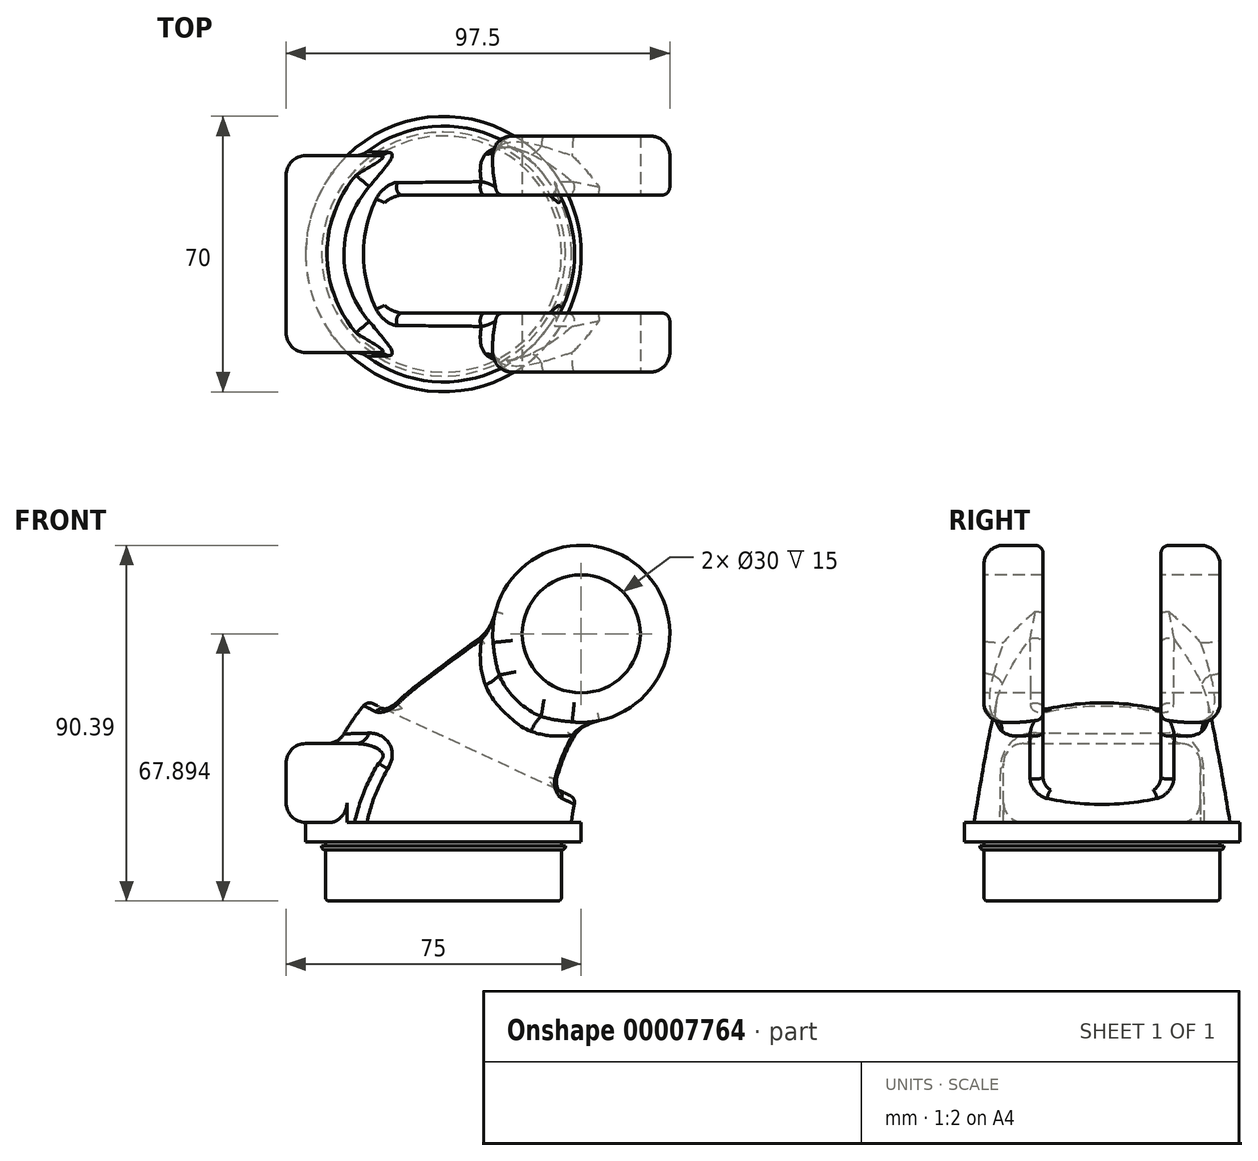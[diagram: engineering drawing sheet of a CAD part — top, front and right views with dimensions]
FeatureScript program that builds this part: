
annotation { "Feature Type Name" : "Feature", "Feature Type Description" : "" }
export const myFeature = defineFeature(function(context is Context, id is Id, definition is map)
    precondition{}
    {
        {
            var Q0;
            Q0=qCreatedBy(makeId("Top.planeOp"),FACE);
            var sketch = newSketch(context, id + "F0", { "sketchPlane" : qUnion([Q0])});
            skCircle(sketch, "E0", {"center": v(0, 0) * mm, "radius": 35 * mm});
            skSolve(sketch);
        }
        {
            var Q0;
            Q0 = qSketchRegion(id + "F0", true);
            extrude(context, id + "F1", {"entities" : qUnion([Q0]), "depth" : 5 * mm});
        }
        {
            var Q0;
            Q0=qCreatedBy(makeId("Front.planeOp"),FACE);
            var sketch = newSketch(context, id + "F2", { "sketchPlane" : qUnion([Q0])});
            skArc(sketch, "E1", {"start": v(17.6, 38.3) * mm, "mid": v(5.55, 23.37) * mm, "end": v(0, 5) * mm});
            skLineSegment(sketch, "E2", {"start": v(17.6, 38.3) * mm, "end": v(35, 52.9) * mm});
            skSolve(sketch);
        }
        {
            var Q0;
            Q0=sQuery(id+"F2.wireOp",EDGE,"E2");
            var Q1;
            Q1=sQuery(id+"F2.wireOp",VERTEX,"E2.end");
            cPlane(context, id + "F3", {"entities" : qUnion([Q0, Q1]), "cplaneType" : CPlaneType.LINE_POINT, "offset" : 150 * mm, "width" : 150 * mm, "height" : 150 * mm});
        }
        {
            var Q0;
            Q0=makeQuery(id+"F1.opExtrude","CAP_FACE",FACE,{"disambiguationData":[OSD([sQuery(id+"F0.wireOp",EDGE,"E0")])],"isStart":false});
            var sketch = newSketch(context, id + "F4", { "sketchPlane" : qUnion([Q0])});
            skCircle(sketch, "E3", {"center": v(0, 0) * mm, "radius": 32.5 * mm});
            skSolve(sketch);
        }
        {
            var Q0;
            Q0=qCreatedBy(id+"F3.planeOp",FACE);
            var sketch = newSketch(context, id + "F5", { "sketchPlane" : qUnion([Q0])});
            skCircle(sketch, "E4", {"center": v(0, 18.02) * mm, "radius": 22.5 * mm});
            skSolve(sketch);
        }
        {
            var Q0;
            Q0=qCreatedBy(makeId("Front.planeOp"),FACE);
            var sketch = newSketch(context, id + "F6", { "sketchPlane" : qUnion([Q0])});
            skArc(sketch, "E5", {"start": v(-13.25, 41.78) * mm, "mid": v(-26.5, 25.3) * mm, "end": v(-32.5, 5) * mm});
            skLineSegment(sketch, "E6", {"start": v(-13.25, 41.78) * mm, "end": v(20.54, 70.13) * mm});
            skSolve(sketch);
        }
        {
            var Q0;
            Q0=qCreatedBy(makeId("Front.planeOp"),FACE);
            var sketch = newSketch(context, id + "F7", { "sketchPlane" : qUnion([Q0])});
            skArc(sketch, "E7", {"start": v(48.46, 34.82) * mm, "mid": v(37.6, 21.45) * mm, "end": v(32.5, 5) * mm});
            skLineSegment(sketch, "E8", {"start": v(48.46, 34.82) * mm, "end": v(49.46, 35.66) * mm});
            skSolve(sketch);
        }
        {
            var Q1;
            Q1=makeQuery(id+"F4.imprint","IMPRINT",FACE,{"disambiguationData":[TD([[makeQuery(id+"F4.imprint","IMPRINT",EDGE,{"derivedFrom":sQuery(id+"F4.wireOp",EDGE,"E3")}),1.0]])]});
            var Q2;
            Q2=makeQuery(id+"F5.imprint","IMPRINT",FACE,{"disambiguationData":[TD([[makeQuery(id+"F5.imprint","IMPRINT",EDGE,{"derivedFrom":sQuery(id+"F5.wireOp",EDGE,"E4")}),1.0]])]});
            var Q3;
            Q3 = qBodyType(qCreatedBy(id + "F6" ,EDGE), BodyType.WIRE);
            var Q4;
            Q4 = qBodyType(qCreatedBy(id + "F7" ,EDGE), BodyType.WIRE);
            loft(context, id + "F8", {"operationType" : NewBodyOperationType.ADD, "addGuides" : true, "sheetProfilesArray" : [{ "sheetProfileEntities" : qUnion([Q1]) }, { "sheetProfileEntities" : qUnion([Q2]) }], "guidesArray" : [{ "guideEntities" : qUnion([Q3]), "guideDerivativeType" : LoftGuideDerivativeType.DEFAULT, "guideDerivativeMagnitude" : 1 }, { "guideEntities" : qUnion([Q4]), "guideDerivativeType" : LoftGuideDerivativeType.DEFAULT, "guideDerivativeMagnitude" : 1 }]});
        }
        {
            var Q0;
            Q0=qCreatedBy(makeId("Front.planeOp"),FACE);
            var sketch = newSketch(context, id + "F9", { "sketchPlane" : qUnion([Q0])});
            skLineSegment(sketch, "E9", {"start": v(20.54, 70.13) * mm, "end": v(49.46, 35.66) * mm, "construction": true});
            skCircle(sketch, "E10", {"center": v(35, 52.9) * mm, "radius": 22.5 * mm});
            skSolve(sketch);
        }
        {
            var Q0;
            Q0 = qSketchRegion(id + "F9", true);
            extrude(context, id + "F10", {"entities" : qUnion([Q0]), "operationType" : NewBodyOperationType.ADD, "endBound" : BoundingType.SYMMETRIC, "depth" : 60 * mm});
        }
        {
            var Q0;
            Q0=makeQuery(id+"F10.boolean.opBoolean","INTERSECT",EDGE,{"derivedFrom":[makeQuery(id+"F8.opLoft","SWEPT_FACE",FACE,{"disambiguationData":[OSD([sQuery(id+"F4.wireOp",EDGE,"E3"),sQuery(id+"F5.wireOp",EDGE,"E4"),sQuery(id+"F6.wireOp",VERTEX,"E6.start"),sQuery(id+"F6.wireOp",EDGE,"E5"),sQuery(id+"F6.wireOp",EDGE,"E6"),sQuery(id+"F7.wireOp",VERTEX,"E8.start"),sQuery(id+"F7.wireOp",EDGE,"E7"),sQuery(id+"F7.wireOp",EDGE,"E8")])]}),makeQuery(id+"F10.opExtrude","SWEPT_FACE",FACE,{"disambiguationData":[OSD([sQuery(id+"F9.wireOp",EDGE,"E10")])]})]});
            fillet(context, id + "F11", {"entities" : qUnion([Q0]), "radius" : 5 * mm, "tangentPropagation" : true, "allowEdgeOverflow" : false});
        }
        {
            var Q0;
            Q0=makeQuery(id+"F10.opExtrude","CAP_EDGE",EDGE,{"disambiguationData":[OSD([sQuery(id+"F9.wireOp",EDGE,"E10")])],"isStart":false});
            var Q1;
            Q1=makeQuery(id+"F10.opExtrude","CAP_EDGE",EDGE,{"disambiguationData":[OSD([sQuery(id+"F9.wireOp",EDGE,"E10")])],"isStart":true});
            fillet(context, id + "F12", {"entities" : qUnion([Q0, Q1]), "radius" : 5 * mm, "tangentPropagation" : true, "allowEdgeOverflow" : false});
        }
        {
            var Q0;
            Q0=makeQuery(id+"F10.opExtrude","CAP_FACE",FACE,{"disambiguationData":[OSD([sQuery(id+"F9.wireOp",EDGE,"E10")])],"isStart":false});
            var sketch = newSketch(context, id + "F13", { "sketchPlane" : qUnion([Q0])});
            skCircle(sketch, "E11", {"center": v(35, 52.9) * mm, "radius": 15 * mm});
            skSolve(sketch);
        }
        {
            var Q0;
            Q0 = qSketchRegion(id + "F13", true);
            extrude(context, id + "F14", {"entities" : qUnion([Q0]), "operationType" : NewBodyOperationType.REMOVE, "endBound" : BoundingType.THROUGH_ALL, "oppositeDirection" : true, "depth" : 25 * mm});
        }
        {
            var Q0;
            Q0=qCreatedBy(makeId("Right.planeOp"),FACE);
            var sketch = newSketch(context, id + "F15", { "sketchPlane" : qUnion([Q0])});
            skLineSegment(sketch, "E12.rect.bottom", {"start": v(-25, 5) * mm, "end": v(25, 5) * mm});
            skLineSegment(sketch, "E12.rect.top", {"start": v(-25, 25) * mm, "end": v(25, 25) * mm});
            skLineSegment(sketch, "E12.rect.left", {"start": v(-25, 5) * mm, "end": v(-25, 25) * mm});
            skLineSegment(sketch, "E12.rect.right", {"start": v(25, 5) * mm, "end": v(25, 25) * mm});
            skPoint(sketch, "E12.rect.middle", {"position": v(0, 15) * mm});
            skSolve(sketch);
        }
        {
            var Q0;
            Q0 = qSketchRegion(id + "F15", true);
            extrude(context, id + "F16", {"entities" : qUnion([Q0]), "operationType" : NewBodyOperationType.ADD, "oppositeDirection" : true, "depth" : 40 * mm});
        }
        {
            var Q0;
            Q0=makeQuery(id+"F16.boolean.opBoolean","INTERSECT",EDGE,{"derivedFrom":[makeQuery(id+"F8.opLoft","SWEPT_FACE",FACE,{"disambiguationData":[OSD([sQuery(id+"F4.wireOp",EDGE,"E3"),sQuery(id+"F5.wireOp",EDGE,"E4"),sQuery(id+"F6.wireOp",VERTEX,"E6.start"),sQuery(id+"F6.wireOp",EDGE,"E5"),sQuery(id+"F6.wireOp",EDGE,"E6"),sQuery(id+"F7.wireOp",VERTEX,"E8.start"),sQuery(id+"F7.wireOp",EDGE,"E7"),sQuery(id+"F7.wireOp",EDGE,"E8")])]}),makeQuery(id+"F16.opExtrude","SWEPT_FACE",FACE,{"disambiguationData":[OSD([sQuery(id+"F15.wireOp",EDGE,"E12.rect.top")])]})]});
            var Q1;
            Q1=makeQuery(id+"F16.boolean.opBoolean","INTERSECT",EDGE,{"derivedFrom":[makeQuery(id+"F8.opLoft","SWEPT_FACE",FACE,{"disambiguationData":[OSD([sQuery(id+"F4.wireOp",EDGE,"E3"),sQuery(id+"F5.wireOp",EDGE,"E4"),sQuery(id+"F6.wireOp",VERTEX,"E6.start"),sQuery(id+"F6.wireOp",EDGE,"E5"),sQuery(id+"F6.wireOp",EDGE,"E6"),sQuery(id+"F7.wireOp",VERTEX,"E8.start"),sQuery(id+"F7.wireOp",EDGE,"E7"),sQuery(id+"F7.wireOp",EDGE,"E8")])]}),makeQuery(id+"F16.opExtrude","SWEPT_FACE",FACE,{"disambiguationData":[OSD([sQuery(id+"F15.wireOp",EDGE,"E12.rect.right")])]})]});
            var Q2;
            Q2=makeQuery(id+"F16.boolean.opBoolean","INTERSECT",EDGE,{"derivedFrom":[makeQuery(id+"F8.opLoft","SWEPT_FACE",FACE,{"disambiguationData":[OSD([sQuery(id+"F4.wireOp",EDGE,"E3"),sQuery(id+"F5.wireOp",EDGE,"E4"),sQuery(id+"F6.wireOp",VERTEX,"E6.start"),sQuery(id+"F6.wireOp",EDGE,"E5"),sQuery(id+"F6.wireOp",EDGE,"E6"),sQuery(id+"F7.wireOp",VERTEX,"E8.start"),sQuery(id+"F7.wireOp",EDGE,"E7"),sQuery(id+"F7.wireOp",EDGE,"E8")])]}),makeQuery(id+"F16.opExtrude","SWEPT_FACE",FACE,{"disambiguationData":[OSD([sQuery(id+"F15.wireOp",EDGE,"E12.rect.left")])]})]});
            var Q3;
            Q3=makeQuery(id+"F16.opExtrude","SWEPT_EDGE",EDGE,{"disambiguationData":[OSD([sQuery(id+"F15.wireOp",EDGE,"E12.rect.top"),sQuery(id+"F15.wireOp",EDGE,"E12.rect.right")])]});
            var Q4;
            Q4=makeQuery(id+"F16.opExtrude","SWEPT_EDGE",EDGE,{"disambiguationData":[OSD([sQuery(id+"F15.wireOp",EDGE,"E12.rect.top"),sQuery(id+"F15.wireOp",EDGE,"E12.rect.left")])]});
            var Q5;
            {var subQ0=sQuery(id+"F15.wireOp",EDGE,"E12.rect.bottom");var subQ1=sQuery(id+"F15.wireOp",EDGE,"E12.rect.right");Q5=makeQuery(id+"F16.boolean.opBoolean","SPLIT",EDGE,{"disambiguationData":[TD([makeQuery(id+"F16.opExtrude","CAP_FACE",FACE,{"disambiguationData":[OSD([subQ0,sQuery(id+"F15.wireOp",EDGE,"E12.rect.top"),sQuery(id+"F15.wireOp",EDGE,"E12.rect.left"),subQ1])],"isStart":false})])],"derivedFrom":makeQuery(id+"F16.opExtrude","SWEPT_EDGE",EDGE,{"disambiguationData":[OSD([subQ0,subQ1])]})});}
            var Q6;
            {var subQ0=sQuery(id+"F15.wireOp",EDGE,"E12.rect.bottom");var subQ1=sQuery(id+"F15.wireOp",EDGE,"E12.rect.left");Q6=makeQuery(id+"F16.boolean.opBoolean","SPLIT",EDGE,{"disambiguationData":[TD([makeQuery(id+"F16.opExtrude","CAP_FACE",FACE,{"disambiguationData":[OSD([subQ0,sQuery(id+"F15.wireOp",EDGE,"E12.rect.top"),subQ1,sQuery(id+"F15.wireOp",EDGE,"E12.rect.right")])],"isStart":false})])],"derivedFrom":makeQuery(id+"F16.opExtrude","SWEPT_EDGE",EDGE,{"disambiguationData":[OSD([subQ0,subQ1])]})});}
            var Q7;
            Q7=makeQuery(id+"F16.opExtrude","CAP_EDGE",EDGE,{"disambiguationData":[OSD([sQuery(id+"F15.wireOp",EDGE,"E12.rect.top")])],"isStart":false});
            var Q8;
            Q8=makeQuery(id+"F16.opExtrude","CAP_EDGE",EDGE,{"disambiguationData":[OSD([sQuery(id+"F15.wireOp",EDGE,"E12.rect.right")])],"isStart":false});
            var Q9;
            Q9=makeQuery(id+"F16.opExtrude","CAP_EDGE",EDGE,{"disambiguationData":[OSD([sQuery(id+"F15.wireOp",EDGE,"E12.rect.bottom")])],"isStart":false});
            var Q10;
            Q10=makeQuery(id+"F16.opExtrude","CAP_EDGE",EDGE,{"disambiguationData":[OSD([sQuery(id+"F15.wireOp",EDGE,"E12.rect.left")])],"isStart":false});
            fillet(context, id + "F17", {"entities" : qUnion([Q0, Q1, Q2, Q3, Q4, Q5, Q6, Q7, Q8, Q9, Q10]), "radius" : 5 * mm, "tangentPropagation" : true, "allowEdgeOverflow" : false});
        }
        {
            var Q0;
            Q0=qCreatedBy(makeId("Front.planeOp"),FACE);
            var sketch = newSketch(context, id + "F18", { "sketchPlane" : qUnion([Q0])});
            skLineSegment(sketch, "E13", {"start": v(57.5, 0) * mm, "end": v(-40, 45.46) * mm});
            skArc(sketch, "E14.0", {"start": v(57.5, 52.9) * mm, "mid": v(50.9, 68.8) * mm, "end": v(35, 75.4) * mm});
            skLineSegment(sketch, "E15", {"start": v(57.5, 52.9) * mm, "end": v(57.5, 0) * mm});
            skLineSegment(sketch, "E16", {"start": v(35, 75.4) * mm, "end": v(-40, 75.4) * mm});
            skLineSegment(sketch, "E17", {"start": v(-40, 75.4) * mm, "end": v(-40, 45.46) * mm});
            skSolve(sketch);
        }
        {
            var Q0;
            Q0 = qSketchRegion(id + "F18", true);
            extrude(context, id + "F19", {"entities" : qUnion([Q0]), "operationType" : NewBodyOperationType.REMOVE, "endBound" : BoundingType.SYMMETRIC, "oppositeDirection" : true, "depth" : 30 * mm});
        }
        {
            var Q0;
            {var subQ0=sQuery(id+"F9.wireOp",EDGE,"E10");Q0=makeQuery(id+"F19.boolean.opBoolean","INTERSECT",EDGE,{"derivedFrom":[makeQuery(id+"FLHICm9JkTWU2v4_1.boolean.opBoolean","MERGE",FACE,{"derivedFrom":[makeQuery(id+"F10.opExtrude","SWEPT_FACE",FACE,{"disambiguationData":[OSD([subQ0])]}),makeQuery(id+"FLHICm9JkTWU2v4_1.opExtrude","SWEPT_FACE",FACE,{"disambiguationData":[OSD([subQ0])]})]}),makeQuery(id+"F19.opExtrude","CAP_FACE",FACE,{"disambiguationData":[OSD([sQuery(id+"F18.wireOp",EDGE,"E13"),sQuery(id+"F18.wireOp",EDGE,"E14.0"),sQuery(id+"F18.wireOp",EDGE,"E15"),sQuery(id+"F18.wireOp",EDGE,"E16"),sQuery(id+"F18.wireOp",EDGE,"E17")])],"isStart":true})]});}
            var Q1;
            {var subQ0=sQuery(id+"F9.wireOp",EDGE,"E10");Q1=makeQuery(id+"F19.boolean.opBoolean","INTERSECT",EDGE,{"derivedFrom":[makeQuery(id+"FLHICm9JkTWU2v4_1.boolean.opBoolean","MERGE",FACE,{"derivedFrom":[makeQuery(id+"F10.opExtrude","SWEPT_FACE",FACE,{"disambiguationData":[OSD([subQ0])]}),makeQuery(id+"FLHICm9JkTWU2v4_1.opExtrude","SWEPT_FACE",FACE,{"disambiguationData":[OSD([subQ0])]})]}),makeQuery(id+"F19.opExtrude","CAP_FACE",FACE,{"disambiguationData":[OSD([sQuery(id+"F18.wireOp",EDGE,"E13"),sQuery(id+"F18.wireOp",EDGE,"E14.0"),sQuery(id+"F18.wireOp",EDGE,"E15"),sQuery(id+"F18.wireOp",EDGE,"E16"),sQuery(id+"F18.wireOp",EDGE,"E17")])],"isStart":false})]});}
            var Q2;
            Q2=makeQuery(id+"F19.boolean.opBoolean","INTERSECT",EDGE,{"disambiguationData":[OD(1.0)],"derivedFrom":[makeQuery(id+"F8.opLoft","SWEPT_FACE",FACE,{"disambiguationData":[OSD([sQuery(id+"F4.wireOp",EDGE,"E3"),sQuery(id+"F5.wireOp",EDGE,"E4"),sQuery(id+"F6.wireOp",VERTEX,"E6.start"),sQuery(id+"F6.wireOp",EDGE,"E5"),sQuery(id+"F6.wireOp",EDGE,"E6"),sQuery(id+"F7.wireOp",VERTEX,"E8.start"),sQuery(id+"F7.wireOp",EDGE,"E7"),sQuery(id+"F7.wireOp",EDGE,"E8")])]}),makeQuery(id+"F19.opExtrude","SWEPT_FACE",FACE,{"disambiguationData":[OSD([sQuery(id+"F18.wireOp",EDGE,"E13")])]})]});
            var Q3;
            Q3=makeQuery(id+"F19.boolean.opBoolean","INTERSECT",EDGE,{"disambiguationData":[OD(0.0)],"derivedFrom":[makeQuery(id+"F8.opLoft","SWEPT_FACE",FACE,{"disambiguationData":[OSD([sQuery(id+"F4.wireOp",EDGE,"E3"),sQuery(id+"F5.wireOp",EDGE,"E4"),sQuery(id+"F6.wireOp",VERTEX,"E6.start"),sQuery(id+"F6.wireOp",EDGE,"E5"),sQuery(id+"F6.wireOp",EDGE,"E6"),sQuery(id+"F7.wireOp",VERTEX,"E8.start"),sQuery(id+"F7.wireOp",EDGE,"E7"),sQuery(id+"F7.wireOp",EDGE,"E8")])]}),makeQuery(id+"F19.opExtrude","SWEPT_FACE",FACE,{"disambiguationData":[OSD([sQuery(id+"F18.wireOp",EDGE,"E13")])]})]});
            var Q4;
            Q4=makeQuery(id+"F19.boolean.opBoolean","COPY",EDGE,{"derivedFrom":makeQuery(id+"F19.opExtrude","CAP_EDGE",EDGE,{"disambiguationData":[OSD([sQuery(id+"F18.wireOp",EDGE,"E13")])],"isStart":true})});
            var Q5;
            Q5=makeQuery(id+"F19.boolean.opBoolean","COPY",EDGE,{"derivedFrom":makeQuery(id+"F19.opExtrude","CAP_EDGE",EDGE,{"disambiguationData":[OSD([sQuery(id+"F18.wireOp",EDGE,"E13")])],"isStart":false})});
            fillet(context, id + "F20", {"entities" : qUnion([Q0, Q1, Q2, Q3, Q4, Q5]), "radius" : 2 * mm, "tangentPropagation" : true, "allowEdgeOverflow" : false});
        }
        {
            var Q0;
            Q0=qCreatedBy(makeId("Front.planeOp"),FACE);
            var sketch = newSketch(context, id + "F21", { "sketchPlane" : qUnion([Q0])});
            skLineSegment(sketch, "E18.bottom", {"start": v(0, 0) * mm, "end": v(-30, 0) * mm});
            skLineSegment(sketch, "E18.top", {"start": v(0, -15) * mm, "end": v(-30, -15) * mm});
            skLineSegment(sketch, "E18.left", {"start": v(0, 0) * mm, "end": v(0, -15) * mm});
            skLineSegment(sketch, "E18.right", {"start": v(-30, 0) * mm, "end": v(-30, -1) * mm});
            skLineSegment(sketch, "E19.bottom", {"start": v(-31, -1) * mm, "end": v(-30, -1) * mm});
            skLineSegment(sketch, "E19.top", {"start": v(-31, -2) * mm, "end": v(-30, -2) * mm});
            skLineSegment(sketch, "E19.left", {"start": v(-31, -1) * mm, "end": v(-31, -2) * mm});
            skLineSegment(sketch, "E20.trimOffspring", {"start": v(-30, -2) * mm, "end": v(-30, -15) * mm});
            skSolve(sketch);
        }
        {
            var Q0;
            Q0 = qSketchRegion(id + "F21", true);
            var Q1;
            Q1=sQuery(id+"F21.wireOp",EDGE,"E18.left");
            revolve(context, id + "F22", {"operationType" : NewBodyOperationType.ADD, "entities" : qUnion([Q0]), "axis" : qUnion([Q1]), "revolveType" : RevolveType.FULL});
        }
        {
            var Q0;
            Q0=makeQuery(id+"F22.opRevolve","SWEPT_EDGE",EDGE,{"disambiguationData":[OSD([sQuery(id+"F21.wireOp",EDGE,"E19.top"),sQuery(id+"F21.wireOp",EDGE,"E19.left")])]});
            var Q1;
            Q1=makeQuery(id+"F22.opRevolve","SWEPT_EDGE",EDGE,{"disambiguationData":[OSD([sQuery(id+"F21.wireOp",EDGE,"E18.top"),sQuery(id+"F21.wireOp",EDGE,"E20.trimOffspring")])]});
            fillet(context, id + "F23", {"entities" : qUnion([Q0, Q1]), "radius" : 1 * mm, "allowEdgeOverflow" : false});
        }
    });
